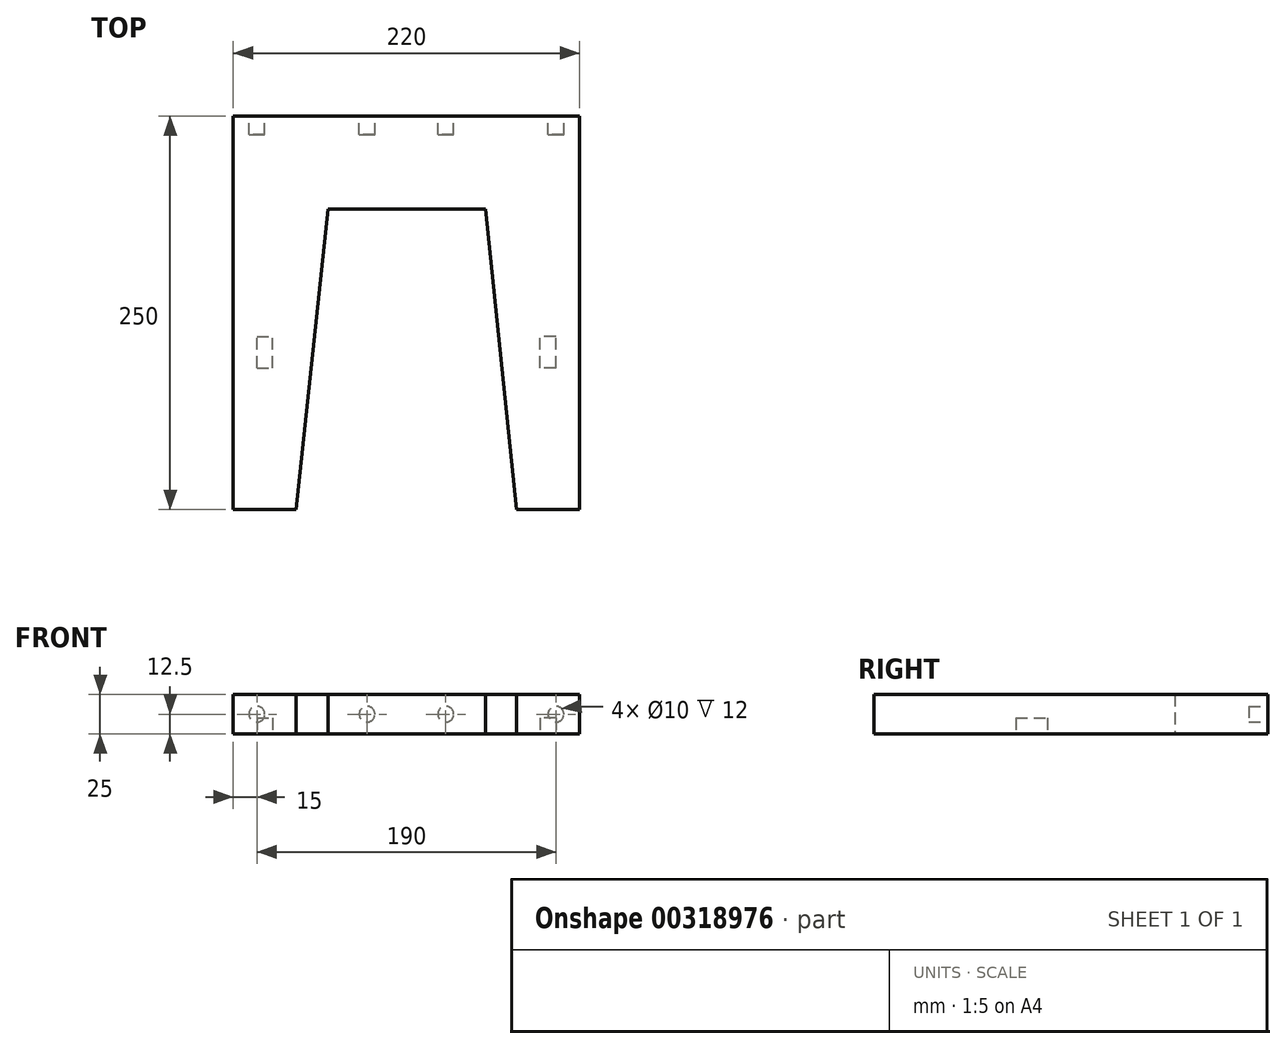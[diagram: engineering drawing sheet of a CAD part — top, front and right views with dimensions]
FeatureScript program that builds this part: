
annotation { "Feature Type Name" : "Feature", "Feature Type Description" : "" }
export const myFeature = defineFeature(function(context is Context, id is Id, definition is map)
    precondition{}
    {
        {
            var Q0;
            Q0=qCreatedBy(makeId("Top.planeOp"),FACE);
            var sketch = newSketch(context, id + "F0", { "sketchPlane" : qUnion([Q0])});
            skLineSegment(sketch, "E0.bottom", {"start": v(110, 125) * mm, "end": v(-110, 125) * mm});
            skLineSegment(sketch, "E0.left", {"start": v(110, 125) * mm, "end": v(110, -125) * mm});
            skLineSegment(sketch, "E0.right", {"start": v(-110, 125) * mm, "end": v(-110, -125) * mm});
            skPoint(sketch, "E0.middle", {"position": v(0, 0) * mm});
            skLineSegment(sketch, "E1", {"start": v(-110, -125) * mm, "end": v(-70, -125) * mm});
            skLineSegment(sketch, "E2", {"start": v(-70, -125) * mm, "end": v(-49.67, 66) * mm});
            skLineSegment(sketch, "E3", {"start": v(-49.67, 66) * mm, "end": v(50.33, 66) * mm});
            skLineSegment(sketch, "E4", {"start": v(50.33, 66) * mm, "end": v(70, -125) * mm});
            skLineSegment(sketch, "E5", {"start": v(70, -125) * mm, "end": v(110, -125) * mm});
            skPoint(sketch, "E6", {"position": v(0.33, 66) * mm});
            skSolve(sketch);
        }
        {
            var Q0;
            Q0 = qSketchRegion(id + "F0", true);
            extrude(context, id + "F1", {"entities" : qUnion([Q0]), "depth" : 25 * mm});
        }
        {
            var Q0;
            Q0=makeQuery(id+"F1.opExtrude","SWEPT_FACE",FACE,{"disambiguationData":[OSD([sQuery(id+"F0.wireOp",EDGE,"E0.bottom")])]});
            var sketch = newSketch(context, id + "F2", { "sketchPlane" : qUnion([Q0])});
            skLineSegment(sketch, "E7", {"start": v(-110, 12.5) * mm, "end": v(110, 12.5) * mm, "construction": true});
            skPoint(sketch, "E8", {"position": v(-25, 12.5) * mm});
            skPoint(sketch, "E9", {"position": v(25, 12.5) * mm});
            skPoint(sketch, "E10", {"position": v(-95, 12.5) * mm});
            skPoint(sketch, "E11", {"position": v(95, 12.5) * mm});
            skCircle(sketch, "E12", {"center": v(95, 12.5) * mm, "radius": 5 * mm});
            skCircle(sketch, "E13", {"center": v(25, 12.5) * mm, "radius": 5 * mm});
            skCircle(sketch, "E14", {"center": v(-25, 12.5) * mm, "radius": 5 * mm});
            skCircle(sketch, "E15", {"center": v(-95, 12.5) * mm, "radius": 5 * mm});
            skSolve(sketch);
        }
        {
            var Q0;
            Q0 = qSketchRegion(id + "F2", true);
            extrude(context, id + "F3", {"entities" : qUnion([Q0]), "operationType" : NewBodyOperationType.REMOVE, "oppositeDirection" : true, "depth" : 12 * mm});
        }
        {
            var Q0;
            Q0=makeQuery(id+"F1.opExtrude","CAP_FACE",FACE,{"disambiguationData":[OSD([sQuery(id+"F0.wireOp",EDGE,"E0.bottom"),sQuery(id+"F0.wireOp",EDGE,"E0.left"),sQuery(id+"F0.wireOp",EDGE,"E0.right"),sQuery(id+"F0.wireOp",EDGE,"E1"),sQuery(id+"F0.wireOp",EDGE,"E2"),sQuery(id+"F0.wireOp",EDGE,"E3"),sQuery(id+"F0.wireOp",EDGE,"E4"),sQuery(id+"F0.wireOp",EDGE,"E5")])],"isStart":true});
            var sketch = newSketch(context, id + "F4", { "sketchPlane" : qUnion([Q0])});
            skLineSegment(sketch, "E16", {"start": v(-95, 125) * mm, "end": v(-95, 35) * mm, "construction": true});
            skLineSegment(sketch, "E17", {"start": v(-95, 35) * mm, "end": v(-110, 35) * mm, "construction": true});
            skLineSegment(sketch, "E18.bottom", {"start": v(-95, 35) * mm, "end": v(-85, 35) * mm});
            skLineSegment(sketch, "E18.top", {"start": v(-95, 15) * mm, "end": v(-85, 15) * mm});
            skLineSegment(sketch, "E18.left", {"start": v(-95, 35) * mm, "end": v(-95, 15) * mm});
            skLineSegment(sketch, "E18.right", {"start": v(-85, 35) * mm, "end": v(-85, 15) * mm});
            skLineSegment(sketch, "E19", {"start": v(0, 0) * mm, "end": v(0, 76.5) * mm});
            skLineSegment(sketch, "E20.MirrorCS", {"start": v(95, 35) * mm, "end": v(85, 35) * mm});
            skLineSegment(sketch, "E21.MirrorCS", {"start": v(95, 15) * mm, "end": v(85, 15) * mm});
            skLineSegment(sketch, "E22.MirrorCS", {"start": v(95, 35) * mm, "end": v(110, 35) * mm, "construction": true});
            skLineSegment(sketch, "E23.MirrorCS", {"start": v(95, 35) * mm, "end": v(95, 15) * mm});
            skLineSegment(sketch, "E24.MirrorCS", {"start": v(85, 35) * mm, "end": v(85, 15) * mm});
            skSolve(sketch);
        }
        {
            var Q0;
            Q0 = qSketchRegion(id + "F4", true);
            extrude(context, id + "F5", {"entities" : qUnion([Q0]), "operationType" : NewBodyOperationType.REMOVE, "oppositeDirection" : true, "depth" : 10 * mm});
        }
    });
